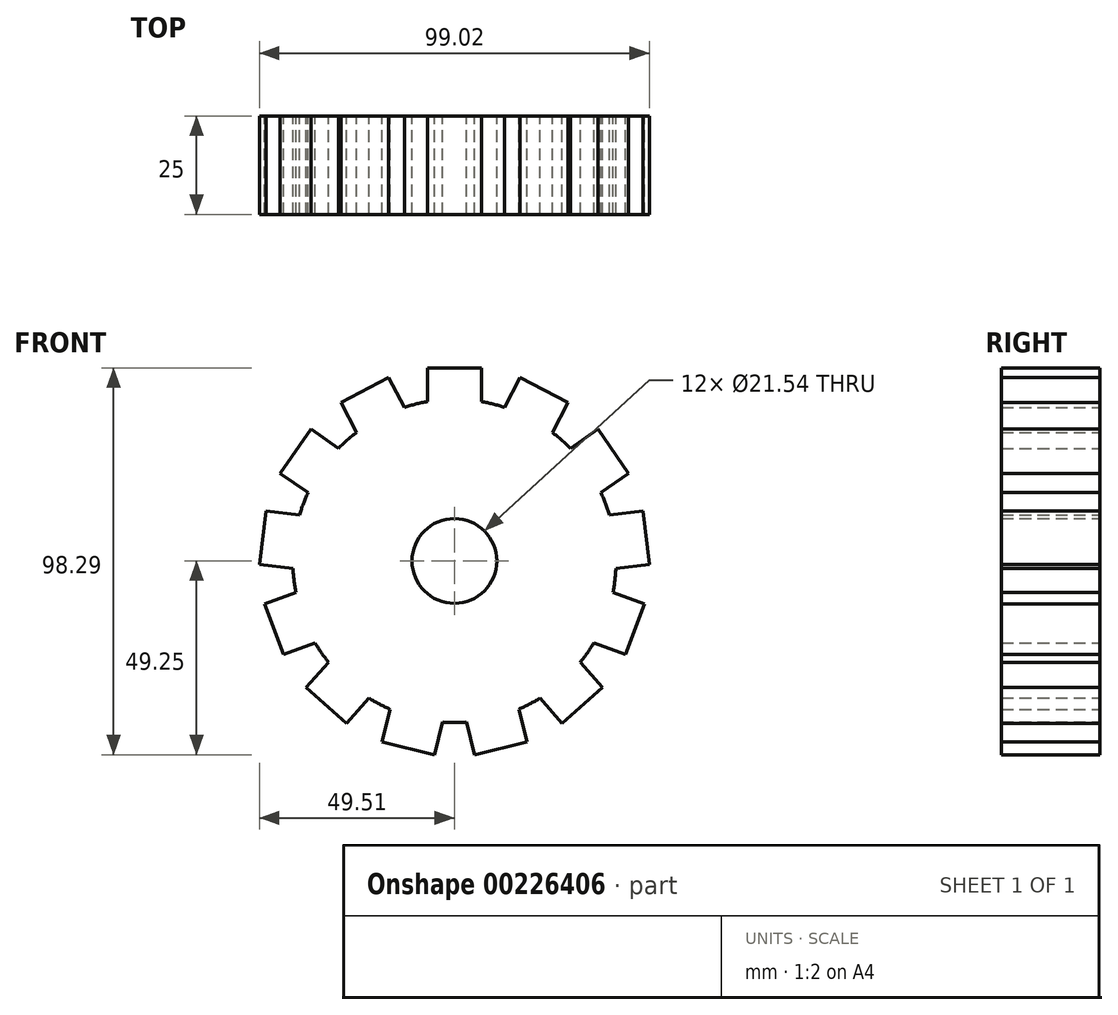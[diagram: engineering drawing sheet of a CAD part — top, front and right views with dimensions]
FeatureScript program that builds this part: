
annotation { "Feature Type Name" : "Feature", "Feature Type Description" : "" }
export const myFeature = defineFeature(function(context is Context, id is Id, definition is map)
    precondition{}
    {
        {
            var Q0;
            Q0=qCreatedBy(makeId("Front.planeOp"),FACE);
            var sketch = newSketch(context, id + "F0", { "sketchPlane" : qUnion([Q0])});
            skCircle(sketch, "E0", {"center": v(0, 0) * mm, "radius": 41.06 * mm});
            skLineSegment(sketch, "E1", {"start": v(0, 0) * mm, "end": v(0, 59.88) * mm, "construction": true});
            skLineSegment(sketch, "E2", {"start": v(-6.86, 40.48) * mm, "end": v(-6.86, 49.04) * mm});
            skLineSegment(sketch, "E3", {"start": v(-6.86, 49.04) * mm, "end": v(6.86, 49.04) * mm});
            skLineSegment(sketch, "E4", {"start": v(6.86, 49.04) * mm, "end": v(6.86, 40.48) * mm});
            skPoint(sketch, "E5", {"position": v(0, 49.04) * mm});
            skLineSegment(sketch, "E6.1.0", {"start": v(-24.88, 32.66) * mm, "end": v(-28.86, 40.23) * mm});
            skLineSegment(sketch, "E6.1.1", {"start": v(-28.86, 40.23) * mm, "end": v(-16.72, 46.6) * mm});
            skLineSegment(sketch, "E6.1.2", {"start": v(-16.72, 46.6) * mm, "end": v(-12.74, 39.03) * mm});
            skLineSegment(sketch, "E6.2.0", {"start": v(-37.21, 17.35) * mm, "end": v(-44.25, 22.21) * mm});
            skLineSegment(sketch, "E6.2.1", {"start": v(-44.25, 22.21) * mm, "end": v(-36.46, 33.5) * mm});
            skLineSegment(sketch, "E6.2.2", {"start": v(-36.46, 33.5) * mm, "end": v(-29.42, 28.64) * mm});
            skLineSegment(sketch, "E6.3.0", {"start": v(-41.01, -1.93) * mm, "end": v(-49.5, -0.9) * mm});
            skLineSegment(sketch, "E6.3.1", {"start": v(-49.5, -0.9) * mm, "end": v(-47.85, 12.72) * mm});
            skLineSegment(sketch, "E6.3.2", {"start": v(-47.85, 12.72) * mm, "end": v(-39.36, 11.69) * mm});
            skLineSegment(sketch, "E6.4.0", {"start": v(-35.42, -20.77) * mm, "end": v(-43.42, -23.8) * mm});
            skLineSegment(sketch, "E6.4.1", {"start": v(-43.42, -23.8) * mm, "end": v(-48.28, -10.98) * mm});
            skLineSegment(sketch, "E6.4.2", {"start": v(-48.28, -10.98) * mm, "end": v(-40.28, -7.94) * mm});
            skLineSegment(sketch, "E6.5.0", {"start": v(-21.71, -34.85) * mm, "end": v(-27.38, -41.25) * mm});
            skLineSegment(sketch, "E6.5.1", {"start": v(-27.38, -41.25) * mm, "end": v(-37.65, -32.16) * mm});
            skLineSegment(sketch, "E6.5.2", {"start": v(-37.65, -32.16) * mm, "end": v(-31.98, -25.75) * mm});
            skLineSegment(sketch, "E6.6.0", {"start": v(-3.03, -40.95) * mm, "end": v(-5.08, -49.25) * mm});
            skLineSegment(sketch, "E6.6.1", {"start": v(-5.08, -49.25) * mm, "end": v(-18.4, -45.97) * mm});
            skLineSegment(sketch, "E6.6.2", {"start": v(-18.4, -45.97) * mm, "end": v(-16.35, -37.66) * mm});
            skLineSegment(sketch, "E6.7.0", {"start": v(16.35, -37.66) * mm, "end": v(18.4, -45.97) * mm});
            skLineSegment(sketch, "E6.7.1", {"start": v(18.4, -45.97) * mm, "end": v(5.08, -49.25) * mm});
            skLineSegment(sketch, "E6.7.2", {"start": v(5.08, -49.25) * mm, "end": v(3.03, -40.95) * mm});
            skLineSegment(sketch, "E6.8.0", {"start": v(31.98, -25.75) * mm, "end": v(37.65, -32.16) * mm});
            skLineSegment(sketch, "E6.8.1", {"start": v(37.65, -32.16) * mm, "end": v(27.38, -41.25) * mm});
            skLineSegment(sketch, "E6.8.2", {"start": v(27.38, -41.25) * mm, "end": v(21.71, -34.85) * mm});
            skLineSegment(sketch, "E6.9.0", {"start": v(40.28, -7.94) * mm, "end": v(48.28, -10.98) * mm});
            skLineSegment(sketch, "E6.9.1", {"start": v(48.28, -10.98) * mm, "end": v(43.42, -23.8) * mm});
            skLineSegment(sketch, "E6.9.2", {"start": v(43.42, -23.8) * mm, "end": v(35.42, -20.77) * mm});
            skLineSegment(sketch, "E6.10.0", {"start": v(39.36, 11.69) * mm, "end": v(47.85, 12.72) * mm});
            skLineSegment(sketch, "E6.10.1", {"start": v(47.85, 12.72) * mm, "end": v(49.5, -0.9) * mm});
            skLineSegment(sketch, "E6.10.2", {"start": v(49.5, -0.9) * mm, "end": v(41.01, -1.93) * mm});
            skLineSegment(sketch, "E6.11.0", {"start": v(29.42, 28.64) * mm, "end": v(36.46, 33.5) * mm});
            skLineSegment(sketch, "E6.11.1", {"start": v(36.46, 33.5) * mm, "end": v(44.25, 22.21) * mm});
            skLineSegment(sketch, "E6.11.2", {"start": v(44.25, 22.21) * mm, "end": v(37.21, 17.35) * mm});
            skLineSegment(sketch, "E6.12.0", {"start": v(12.74, 39.03) * mm, "end": v(16.72, 46.6) * mm});
            skLineSegment(sketch, "E6.12.1", {"start": v(16.72, 46.6) * mm, "end": v(28.86, 40.23) * mm});
            skLineSegment(sketch, "E6.12.2", {"start": v(28.86, 40.23) * mm, "end": v(24.88, 32.66) * mm});
            skCircle(sketch, "E7", {"center": v(0, 0) * mm, "radius": 10.77 * mm});
            skSolve(sketch);
        }
        {
            var Q0;
            Q0 = qSketchRegion(id + "F0", true);
            extrude(context, id + "F1", {"entities" : qUnion([Q0]), "depth" : 25 * mm});
        }
    });
